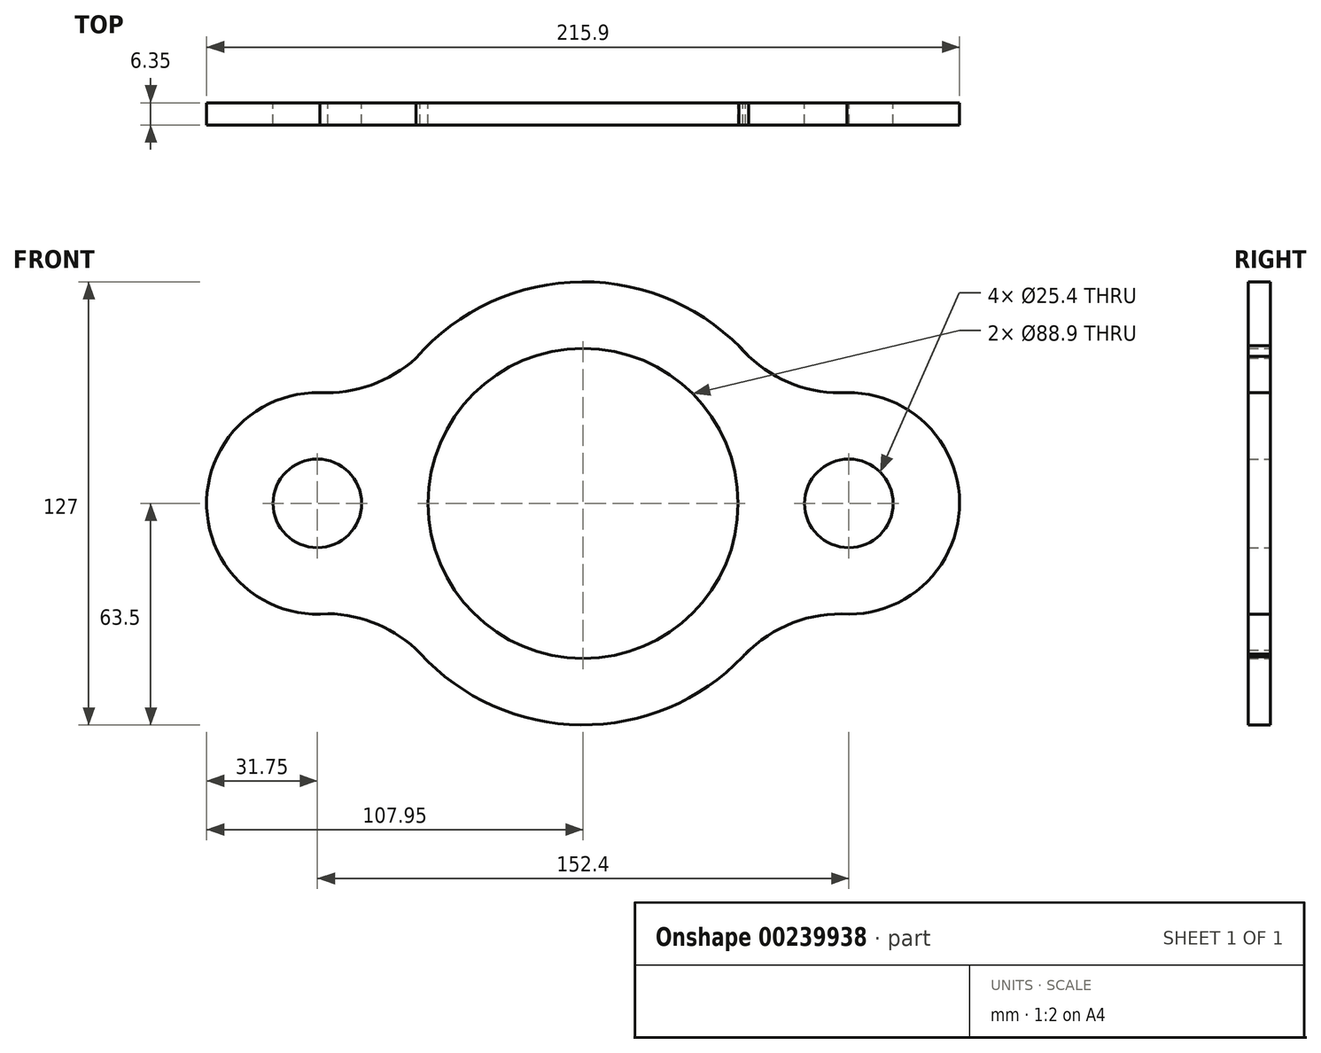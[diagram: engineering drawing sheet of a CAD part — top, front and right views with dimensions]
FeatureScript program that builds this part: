
annotation { "Feature Type Name" : "Feature", "Feature Type Description" : "" }
export const myFeature = defineFeature(function(context is Context, id is Id, definition is map)
    precondition{}
    {
        {
            var Q0;
            Q0=qCreatedBy(makeId("Front.planeOp"),FACE);
            var sketch = newSketch(context, id + "F0", { "sketchPlane" : qUnion([Q0])});
            skArc(sketch, "E0", {"start": v(47.5, 42.13) * mm, "mid": v(-0.32, 63.5) * mm, "end": v(-47.93, 41.65) * mm});
            skCircle(sketch, "E1", {"center": v(0, 0) * mm, "radius": 44.45 * mm});
            skArc(sketch, "E2", {"start": v(73.99, -31.67) * mm, "mid": v(107.94, -0.83) * mm, "end": v(75.65, 31.75) * mm});
            skCircle(sketch, "E3", {"center": v(76.2, 0) * mm, "radius": 12.7 * mm});
            skArc(sketch, "E4", {"start": v(-75.5, 31.74) * mm, "mid": v(-107.93, -1.15) * mm, "end": v(-73.2, -31.6) * mm});
            skCircle(sketch, "E5", {"center": v(-76.2, 0) * mm, "radius": 12.7 * mm});
            skArc(sketch, "E6", {"start": v(47.55, -42.09) * mm, "mid": v(46.66, -43.02) * mm, "end": v(45.8, -43.99) * mm});
            skArc(sketch, "E7", {"start": v(44.66, 45.14) * mm, "mid": v(58.59, 34.82) * mm, "end": v(75.65, 31.75) * mm});
            skArc(sketch, "E8", {"start": v(-75.5, 31.74) * mm, "mid": v(-58.17, 34.97) * mm, "end": v(-44.14, 45.65) * mm});
            skArc(sketch, "E9", {"start": v(-46.76, -42.96) * mm, "mid": v(-58.87, -34.7) * mm, "end": v(-73.2, -31.6) * mm});
            skArc(sketch, "E10.trimOffspring", {"start": v(-46.76, -42.96) * mm, "mid": v(0.59, -63.5) * mm, "end": v(47.55, -42.09) * mm});
            skArc(sketch, "E11", {"start": v(76.27, -31.75) * mm, "mid": v(59.65, -34.42) * mm, "end": v(45.8, -43.99) * mm});
            skSolve(sketch);
        }
        {
            var Q0;
            {var subQ0=sQuery(id+"F0.wireOp",EDGE,"E0");var subQ1=makeQuery(id+"F0.imprint","INTERSECT",VERTEX,{"derivedFrom":[subQ0,sQuery(id+"F0.wireOp",EDGE,"E3")]});Q0=makeQuery(id+"F0.imprint","IMPRINT",FACE,{"disambiguationData":[TD([[makeQuery(id+"F0.imprint","IMPRINT",EDGE,{"disambiguationData":[TD([[subQ1,1.0]])],"derivedFrom":subQ0}),1.0]])]});}
            var Q1;
            {var subQ8=sQuery(id+"F0.wireOp",EDGE,"E3");Q1=makeQuery(id+"F0.imprint","IMPRINT",FACE,{"disambiguationData":[TD([[makeQuery(id+"F0.imprint","IMPRINT",EDGE,{"derivedFrom":subQ8}),-1.0]])]});}
            extrude(context, id + "F1", {"entities" : qUnion([Q0, Q1]), "depth" : 6.35 * mm});
        }
        {
            var Q0;
            {var subQ0=sQuery(id+"F0.wireOp",EDGE,"E0");var subQ1=makeQuery(id+"F0.imprint","INTERSECT",VERTEX,{"derivedFrom":[subQ0,sQuery(id+"F0.wireOp",EDGE,"E5")]});Q0=makeQuery(id+"F0.imprint","IMPRINT",FACE,{"disambiguationData":[TD([[makeQuery(id+"F0.imprint","IMPRINT",EDGE,{"disambiguationData":[TD([[subQ1,1.0]])],"derivedFrom":subQ0}),1.0]])]});}
            var Q1;
            {var subQ8=sQuery(id+"F0.wireOp",EDGE,"E5");Q1=makeQuery(id+"F0.imprint","IMPRINT",FACE,{"disambiguationData":[TD([[makeQuery(id+"F0.imprint","IMPRINT",EDGE,{"derivedFrom":subQ8}),-1.0]])]});}
            extrude(context, id + "F2", {"entities" : qUnion([Q0, Q1]), "depth" : 6.35 * mm});
        }
        {
            var Q0;
            {var subQ0=sQuery(id+"F0.wireOp",EDGE,"E8");var subQ1=sQuery(id+"F0.wireOp",EDGE,"E0");var subQ2=makeQuery(id+"F0.imprint","INTERSECT",VERTEX,{"disambiguationData":[OD(1.0)],"derivedFrom":[subQ1,subQ0]});Q0=makeQuery(id+"F0.imprint","IMPRINT",FACE,{"disambiguationData":[TD([[makeQuery(id+"F0.imprint","IMPRINT",EDGE,{"disambiguationData":[TD([[subQ2,-1.0]])],"derivedFrom":subQ1}),-1.0]])]});}
            var Q1;
            {var subQ6=sQuery(id+"F0.wireOp",EDGE,"E0");var subQ9=sQuery(id+"F0.wireOp",EDGE,"E7");var subQ11=makeQuery(id+"F0.imprint","INTERSECT",VERTEX,{"disambiguationData":[OD(1.0)],"derivedFrom":[subQ6,subQ9]});Q1=makeQuery(id+"F0.imprint","IMPRINT",FACE,{"disambiguationData":[TD([[makeQuery(id+"F0.imprint","IMPRINT",EDGE,{"disambiguationData":[TD([[subQ11,1.0]])],"derivedFrom":subQ6}),1.0]])]});}
            var Q2;
            {var subQ0=sQuery(id+"F0.wireOp",EDGE,"E7");var subQ1=sQuery(id+"F0.wireOp",EDGE,"E0");var subQ2=makeQuery(id+"F0.imprint","INTERSECT",VERTEX,{"disambiguationData":[OD(1.0)],"derivedFrom":[subQ1,subQ0]});Q2=makeQuery(id+"F0.imprint","IMPRINT",FACE,{"disambiguationData":[TD([[makeQuery(id+"F0.imprint","IMPRINT",EDGE,{"disambiguationData":[TD([[subQ2,1.0]])],"derivedFrom":subQ1}),-1.0]])]});}
            extrude(context, id + "F3", {"entities" : qUnion([Q0, Q1, Q2]), "depth" : 6.35 * mm});
        }
    });
